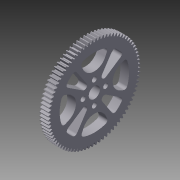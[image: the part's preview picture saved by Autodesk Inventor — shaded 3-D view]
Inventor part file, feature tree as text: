
AUTODESK INVENTOR PART (.ipt)
format: ipt  version: 2014 SP1 (Build 180222100, 222)  size: 717,824 bytes
history: native  units: in
note: dims shown in document units (in); Inventor stores cm internally (conversion verified against a paired STEP export)
features: fillet x3, extrude x2, pattern_circular x2, sketch x2, imported_body x1
ambient origin geometry x8: Origin, YZ Plane, XZ Plane, XY Plane, X Axis, Y Axis, Z Axis, Center Point
bodies: Solid1 (feature_tree)
feature tree (10):
  imported_body  "Base1"
  extrude  "Extrusion1"  Depth=0.25in
  fillet  "Fillet1"  Radius=0.0344in
  pattern_circular  "Circular Pattern1"  [2 undecoded]
  fillet  "Fillet2"  Radius=0.0344in
  extrude  "Extrusion2"  Depth=0.0787in
  fillet  "Fillet3"  Radius=0.125in
  pattern_circular  "Circular Pattern2"  [2 undecoded]
  sketch  "Sketch1"  dims[d0=0.125in d1=0.25in d2=0.0344in]
  sketch  "Sketch2"  dims[d3=0.0344in d4=0.0344in d5=0.0344in d6=0.0787in d7=0.125in d8=0.3937in d9=0.0in d10=0.0787in d11=1.5748in d12=360.0deg d14=0.0787in d15=0.125in d16=0.0687in d17=0.0687in d18=0.341in d19=0.3937in d20=0.0in d21=0.0787in d22=1.5748in d23=360.0deg]
note: 4 required parameter values undecoded (feature->parameter linkage not recoverable at this tier; creation-order binding heuristic only, values carry confidence <= 0.55)
